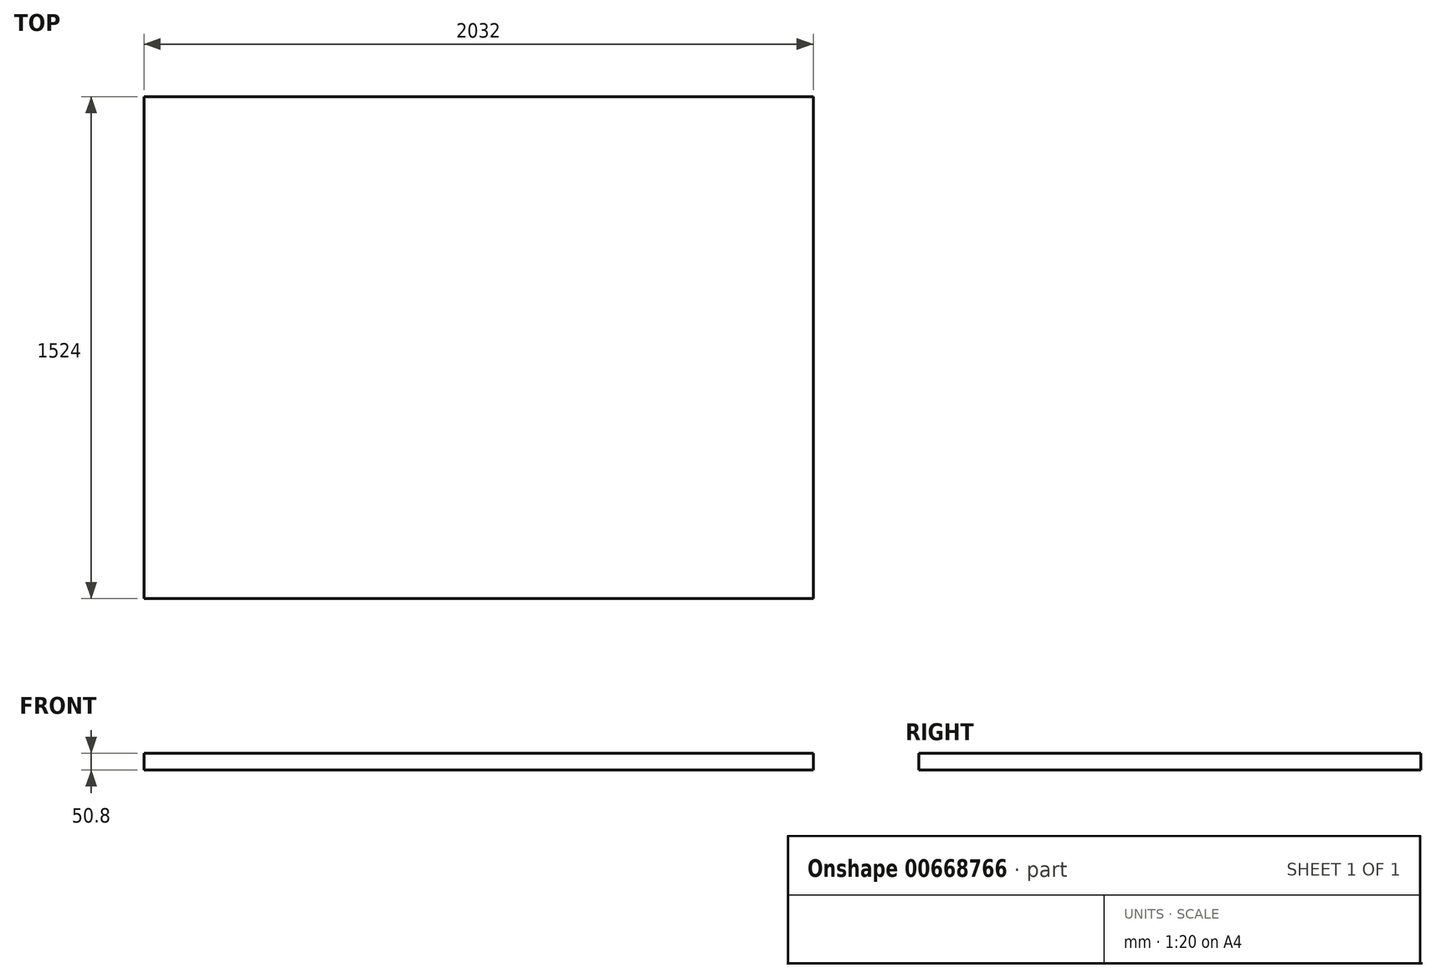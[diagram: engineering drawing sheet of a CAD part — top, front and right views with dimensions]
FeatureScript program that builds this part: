
annotation { "Feature Type Name" : "Feature", "Feature Type Description" : "" }
export const myFeature = defineFeature(function(context is Context, id is Id, definition is map)
    precondition{}
    {
        {
            var Q0;
            Q0=qCreatedBy(makeId("Top.planeOp"),FACE);
            var sketch = newSketch(context, id + "F0", { "sketchPlane" : qUnion([Q0])});
            skLineSegment(sketch, "E0.bottom", {"start": v(-1018.13, 903.66) * mm, "end": v(1013.87, 903.66) * mm});
            skLineSegment(sketch, "E0.top", {"start": v(-1018.13, -620.34) * mm, "end": v(1013.87, -620.34) * mm});
            skLineSegment(sketch, "E0.left", {"start": v(-1018.13, 903.66) * mm, "end": v(-1018.13, -620.34) * mm});
            skLineSegment(sketch, "E0.right", {"start": v(1013.87, 903.66) * mm, "end": v(1013.87, -620.34) * mm});
            skSolve(sketch);
        }
        {
            var Q0;
            Q0=makeQuery(id+"F0.imprint","IMPRINT",FACE,{"disambiguationData":[TD([[makeQuery(id+"F0.imprint","IMPRINT",EDGE,{"derivedFrom":sQuery(id+"F0.wireOp",EDGE,"E0.bottom")}),-1.0]])]});
            extrude(context, id + "F1", {"entities" : qUnion([Q0]), "depth" : 50.8 * mm, "offsetDistance" : 25.4 * mm});
        }
    });
